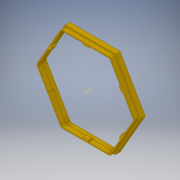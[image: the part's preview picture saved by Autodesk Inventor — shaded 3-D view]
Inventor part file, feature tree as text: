
AUTODESK INVENTOR PART (.ipt)
format: ipt  version: 2019 (Build 230136000, 136)  size: 560,640 bytes
history: native  units: mm
features: projected_geometry x15, extrude x10, sketch x10, pattern_circular x3, fillet x2, other x1
ambient origin geometry x8: Origin, YZ Plane, XZ Plane, XY Plane, X Axis, Y Axis, Z Axis, Center Point
bodies: Solid1 (feature_tree)
feature tree (41):
  extrude  "Extrusion1"  Depth=2.0mm
  extrude  "Extrusion5"  Depth=2.0mm
  extrude  "Extrusion6"  Depth=10.0mm
  fillet  "Fillet1"  [1 undecoded]
  fillet  "Fillet2"  Radius=4.0mm
  extrude  "Extrusion7"  TaperAngle=0.0deg  [1 undecoded]
  extrude  "Extrusion8"  Depth=4.0mm
  other  "Work Axis2"
  pattern_circular  "Circular Pattern1"  [2 undecoded]
  extrude  "Extrusion9"  Depth=10.0mm
  extrude  "Extrusion10"  TaperAngle=0.0deg  [1 undecoded]
  extrude  "Extrusion11"  Depth=10.0mm
  pattern_circular  "Circular Pattern2"  Angle=360.0deg  [1 undecoded]
  extrude  "Extrusion12"  Depth=3.0mm TaperAngle=0.0deg
  pattern_circular  "Circular Pattern3"  [2 undecoded]
  extrude  "Extrusion13"  Depth=10.0mm TaperAngle=0.0deg
  sketch  "Sketch1"  dims[d0=175.0mm d1=2.0mm]
  sketch  "Sketch5"  dims[d2=0.0mm d15=2.0mm]
  projected_geometry  "Projected Loop4"
  sketch  "Sketch7"  dims[d16=2.0mm d17=10.0mm d18=0.0mm d19=4.0mm]
  projected_geometry  "Projected Loop6"
  sketch  "Sketch8"  dims[d20=7.0mm d21=0.0mm]
  sketch  "Sketch9"  dims[d22=10.0mm d23=4.0mm]
  projected_geometry  "Projected Loop7"
  sketch  "Sketch11"  dims[d24=10.0mm]
  projected_geometry  "Projected Loop8"
  sketch  "Sketch12"  dims[d25=3.3mm]
  projected_geometry  "Projected Loop9"
  projected_geometry  "Projected Loop10"
  projected_geometry  "Projected Loop11"
  projected_geometry  "Projected Loop12"
  projected_geometry  "Projected Loop13"
  projected_geometry  "Projected Loop14"
  sketch  "Sketch13"  dims[d26=6.5mm]
  projected_geometry  "Projected Loop15"
  projected_geometry  "Projected Loop16"
  projected_geometry  "Projected Loop17"
  sketch  "Sketch14"  dims[d27=0.0mm]
  projected_geometry  "Projected Loop18"
  sketch  "Sketch15"  dims[d28=4.0mm d29=3.0mm d30=5.0mm d31=0.0mm d32=60.0mm d33=360.0deg d35=3.0mm d36=0.0mm d37=3.0mm d38=0.0mm d39=3.5mm d40=0.0mm d41=60.0mm d42=360.0deg d44=0.7mm d45=0.7mm d46=0.7mm d47=10.0mm d48=0.0mm d49=60.0mm d50=360.0deg d52=175.0mm d53=10.0mm d54=0.0mm]
  projected_geometry  "Projected Loop19"
note: 8 required parameter values undecoded (feature->parameter linkage not recoverable at this tier; creation-order binding heuristic only, values carry confidence <= 0.55)
